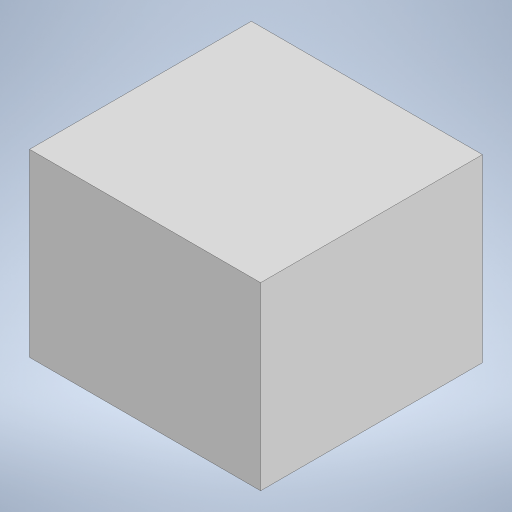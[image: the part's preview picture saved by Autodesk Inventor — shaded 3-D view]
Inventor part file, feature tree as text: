
AUTODESK INVENTOR PART (.ipt)
format: ipt  version: 2023.5 (Build 275446000, 446)  size: 144,896 bytes
history: native  units: mm
features: extrude x1, sketch x1
ambient origin geometry x8: Origin, YZ Plane, XZ Plane, XY Plane, X Axis, Y Axis, Z Axis, Center Point
bodies: 实体1 (feature_tree)
feature tree (2):
  extrude  "拉伸1"  Depth=48.0mm
  sketch  "草图1"  dims[d0=39.0mm d1=48.0mm d2=50.0mm d3=0.0mm]
